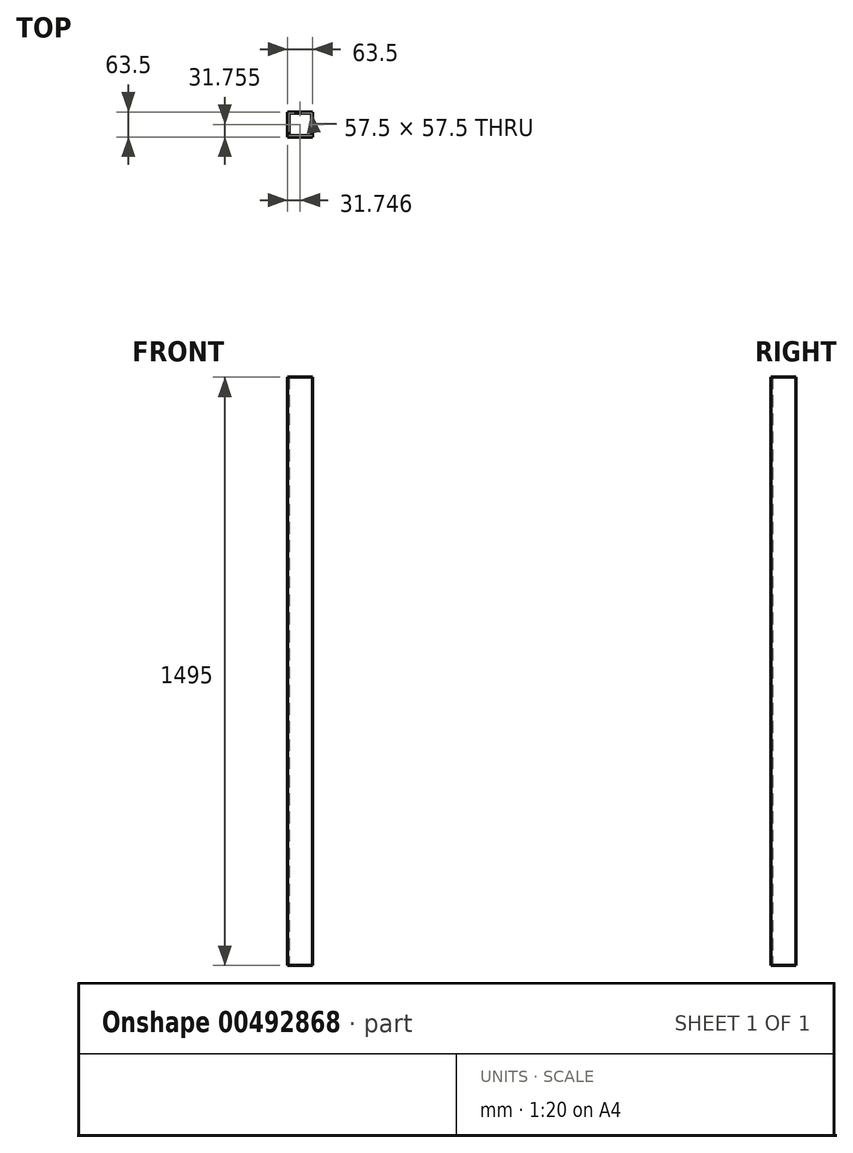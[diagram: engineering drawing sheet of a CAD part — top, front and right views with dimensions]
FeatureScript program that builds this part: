
annotation { "Feature Type Name" : "Feature", "Feature Type Description" : "" }
export const myFeature = defineFeature(function(context is Context, id is Id, definition is map)
    precondition{}
    {
        {
            var Q0;
            Q0=qCreatedBy(makeId("Top.planeOp"),FACE);
            var sketch = newSketch(context, id + "F0", { "sketchPlane" : qUnion([Q0])});
            skLineSegment(sketch, "E0.bottom", {"start": v(-23.06, 14.38) * mm, "end": v(34.44, 14.38) * mm});
            skLineSegment(sketch, "E0.top", {"start": v(-23.06, -43.12) * mm, "end": v(34.44, -43.12) * mm});
            skLineSegment(sketch, "E0.left", {"start": v(-23.06, 14.38) * mm, "end": v(-23.06, -43.12) * mm});
            skLineSegment(sketch, "E0.right", {"start": v(34.44, 14.38) * mm, "end": v(34.44, -43.12) * mm});
            skLineSegment(sketch, "E1.bottom", {"start": v(-26.06, 17.38) * mm, "end": v(37.44, 17.38) * mm});
            skLineSegment(sketch, "E1.top", {"start": v(-26.06, -46.12) * mm, "end": v(37.44, -46.12) * mm});
            skLineSegment(sketch, "E1.left", {"start": v(-26.06, 17.38) * mm, "end": v(-26.06, -46.12) * mm});
            skLineSegment(sketch, "E1.right", {"start": v(37.44, 17.38) * mm, "end": v(37.44, -46.12) * mm});
            skSolve(sketch);
        }
        {
            var Q0;
            Q0 = qSketchRegion(id + "F0", true);
            extrude(context, id + "F1", {"entities" : qUnion([Q0]), "depth" : 1495 * mm});
        }
    });
